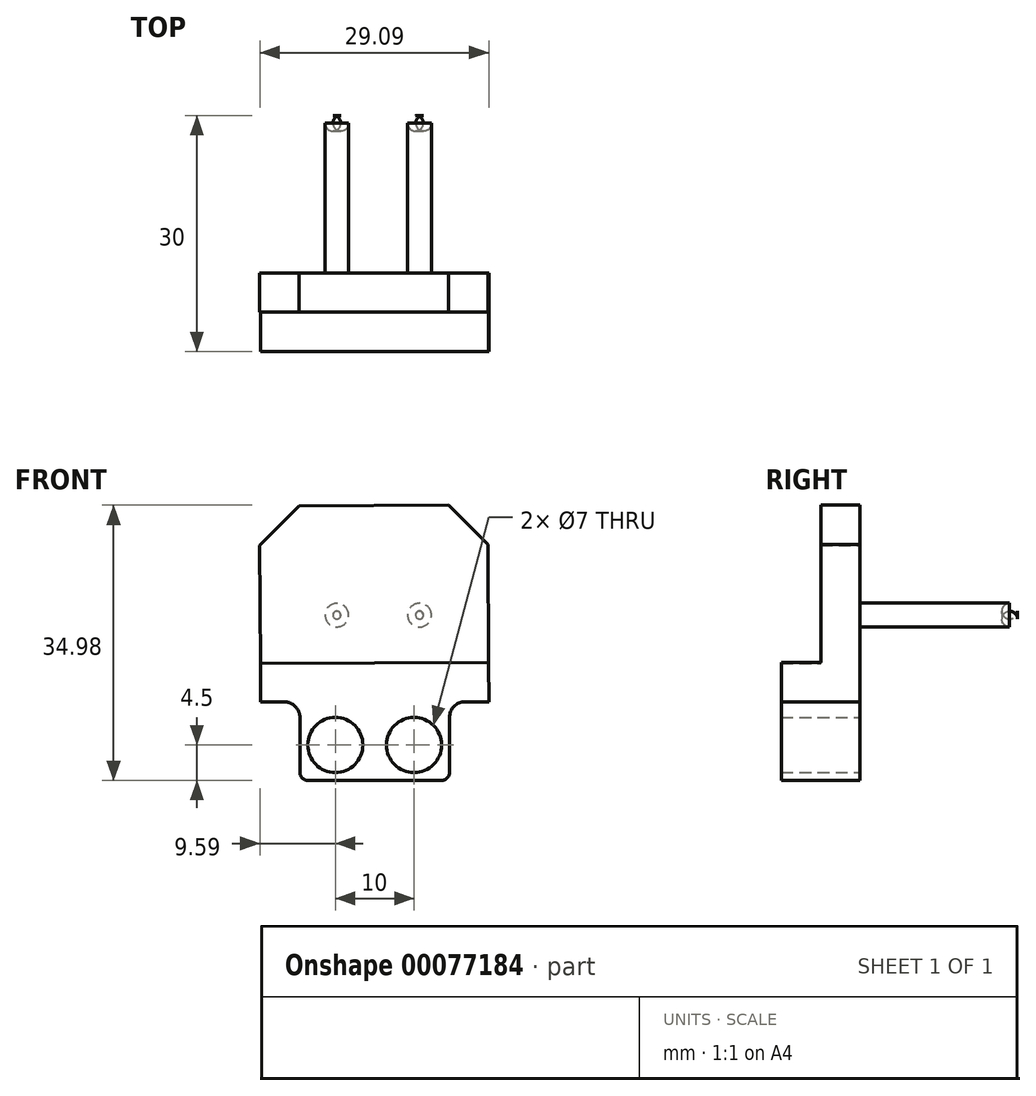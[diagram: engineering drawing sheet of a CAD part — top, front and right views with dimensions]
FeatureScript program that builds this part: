
annotation { "Feature Type Name" : "Feature", "Feature Type Description" : "" }
export const myFeature = defineFeature(function(context is Context, id is Id, definition is map)
    precondition{}
    {
        {
            var Q0;
            Q0=qCreatedBy(makeId("Front.planeOp"),FACE);
            var sketch = newSketch(context, id + "F0", { "sketchPlane" : qUnion([Q0])});
            skLineSegment(sketch, "E0.bottom", {"start": v(0, 0) * mm, "end": v(19, 0) * mm});
            skLineSegment(sketch, "E0.top", {"start": v(0, 10) * mm, "end": v(19, 10) * mm});
            skLineSegment(sketch, "E0.left", {"start": v(0, 0) * mm, "end": v(0, 10) * mm});
            skLineSegment(sketch, "E0.right", {"start": v(19, 0) * mm, "end": v(19, 10) * mm});
            skLineSegment(sketch, "E1", {"start": v(19, 10) * mm, "end": v(24, 10) * mm});
            skLineSegment(sketch, "E2", {"start": v(24, 10) * mm, "end": v(23.98, 15) * mm});
            skLineSegment(sketch, "E3", {"start": v(23.98, 15) * mm, "end": v(-5.02, 14.87) * mm});
            skLineSegment(sketch, "E4", {"start": v(-5.02, 14.87) * mm, "end": v(-5, 9.97) * mm});
            skLineSegment(sketch, "E5", {"start": v(-5, 9.97) * mm, "end": v(0, 10) * mm});
            skCircle(sketch, "E6", {"center": v(4.5, 4.5) * mm, "radius": 3.5 * mm});
            skCircle(sketch, "E7", {"center": v(14.5, 4.5) * mm, "radius": 3.5 * mm});
            skSolve(sketch);
        }
        {
            var Q0;
            Q0=qSketchRegion(id+"F0",true);
            extrude(context, id + "F1", {"entities" : qUnion([Q0]), "depth" : 10 * mm});
        }
        {
            var Q0;
            Q0=makeQuery(id+"F1.opExtrude","SWEPT_FACE",FACE,{"disambiguationData":[OSD([sQuery(id+"F0.wireOp",EDGE,"E3")])]});
            var sketch = newSketch(context, id + "F2", { "sketchPlane" : qUnion([Q0])});
            skLineSegment(sketch, "E8.bottom", {"start": v(-4.95, 0) * mm, "end": v(24.05, 0) * mm});
            skLineSegment(sketch, "E8.top", {"start": v(-4.95, -5) * mm, "end": v(24.05, -5) * mm});
            skLineSegment(sketch, "E8.left", {"start": v(-4.95, 0) * mm, "end": v(-4.95, -5) * mm});
            skLineSegment(sketch, "E8.right", {"start": v(24.05, 0) * mm, "end": v(24.05, -5) * mm});
            skSolve(sketch);
        }
        {
            var Q0;
            Q0=qSketchRegion(id+"F2",true);
            extrude(context, id + "F3", {"entities" : qUnion([Q0]), "operationType" : NewBodyOperationType.ADD, "depth" : 20 * mm});
        }
        {
            var Q0;
            Q0=makeQuery(id+"F3.opExtrude","SWEPT_FACE",FACE,{"disambiguationData":[OSD([sQuery(id+"F2.wireOp",EDGE,"E8.top")])]});
            var sketch = newSketch(context, id + "F4", { "sketchPlane" : qUnion([Q0])});
            skCircle(sketch, "E9", {"center": v(4.7, 21) * mm, "radius": 1.5 * mm});
            skCircle(sketch, "E10", {"center": v(15.2, 21) * mm, "radius": 1.51 * mm});
            skSolve(sketch);
        }
        {
            var Q0;
            Q0=qSketchRegion(id+"F4",true);
            extrude(context, id + "F5", {"entities" : qUnion([Q0]), "operationType" : NewBodyOperationType.ADD, "oppositeDirection" : true, "depth" : 25 * mm});
        }
        {
            var Q0;
            Q0=makeQuery(id+"F3.opExtrude","CAP_EDGE",EDGE,{"disambiguationData":[OSD([sQuery(id+"F2.wireOp",EDGE,"E8.left")])],"isStart":false});
            var Q1;
            Q1=makeQuery(id+"F3.opExtrude","CAP_EDGE",EDGE,{"disambiguationData":[OSD([sQuery(id+"F2.wireOp",EDGE,"E8.right")])],"isStart":false});
            chamfer(context, id + "F6", {"entities" : qUnion([Q0, Q1]), "width" : 5 * mm, "tangentPropagation" : true});
        }
        {
            var Q0;
            Q0=makeQuery(id+"F5.opExtrude","CAP_EDGE",EDGE,{"disambiguationData":[OSD([sQuery(id+"F4.wireOp",EDGE,"E9")])],"isStart":false});
            var Q1;
            Q1=makeQuery(id+"F5.opExtrude","CAP_EDGE",EDGE,{"disambiguationData":[OSD([sQuery(id+"F4.wireOp",EDGE,"E10")])],"isStart":false});
            fillet(context, id + "F7", {"entities" : qUnion([Q0, Q1]), "radius" : 1 * mm, "tangentPropagation" : true, "allowEdgeOverflow" : false});
        }
        {
            var Q0;
            Q0=makeQuery(id+"F1.opExtrude","SWEPT_EDGE",EDGE,{"disambiguationData":[OSD([sQuery(id+"F0.wireOp",EDGE,"E0.bottom"),sQuery(id+"F0.wireOp",EDGE,"E0.right")])]});
            var Q1;
            Q1=makeQuery(id+"F1.opExtrude","SWEPT_EDGE",EDGE,{"disambiguationData":[OSD([sQuery(id+"F0.wireOp",EDGE,"E0.bottom"),sQuery(id+"F0.wireOp",EDGE,"E0.left")])]});
            fillet(context, id + "F8", {"entities" : qUnion([Q0, Q1]), "radius" : 1 * mm, "tangentPropagation" : true, "allowEdgeOverflow" : false});
        }
        {
            var Q0;
            Q0=makeQuery(id+"F1.opExtrude","SWEPT_EDGE",EDGE,{"disambiguationData":[OSD([sQuery(id+"F0.wireOp",EDGE,"E0.top"),sQuery(id+"F0.wireOp",EDGE,"E0.right"),sQuery(id+"F0.wireOp",EDGE,"E1")])]});
            var Q1;
            Q1=makeQuery(id+"F1.opExtrude","SWEPT_EDGE",EDGE,{"disambiguationData":[OSD([sQuery(id+"F0.wireOp",EDGE,"E0.top"),sQuery(id+"F0.wireOp",EDGE,"E0.left"),sQuery(id+"F0.wireOp",EDGE,"E5")])]});
            fillet(context, id + "F9", {"entities" : qUnion([Q0, Q1]), "radius" : 2 * mm, "tangentPropagation" : true, "allowEdgeOverflow" : false});
        }
    });
